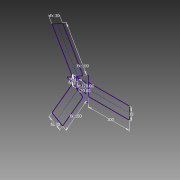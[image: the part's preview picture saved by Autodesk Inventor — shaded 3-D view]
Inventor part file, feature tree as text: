
AUTODESK INVENTOR PART (.ipt)
format: ipt  version: 2015 (Build 190159000, 159)  size: 77,824 bytes
history: native  units: mm
features: sketch x1
ambient origin geometry x8: Origin, YZ Plane, XZ Plane, XY Plane, X Axis, Y Axis, Z Axis, Center Point
feature tree (1):
  sketch  "Sketch1"  dims[d1=25.4mm d2=30.0mm d3=100.0mm d4=30.0mm d5=100.0mm d6=120.0deg d7=30.0mm d8=100.0mm d9=120.0deg d10=23.0mm]
